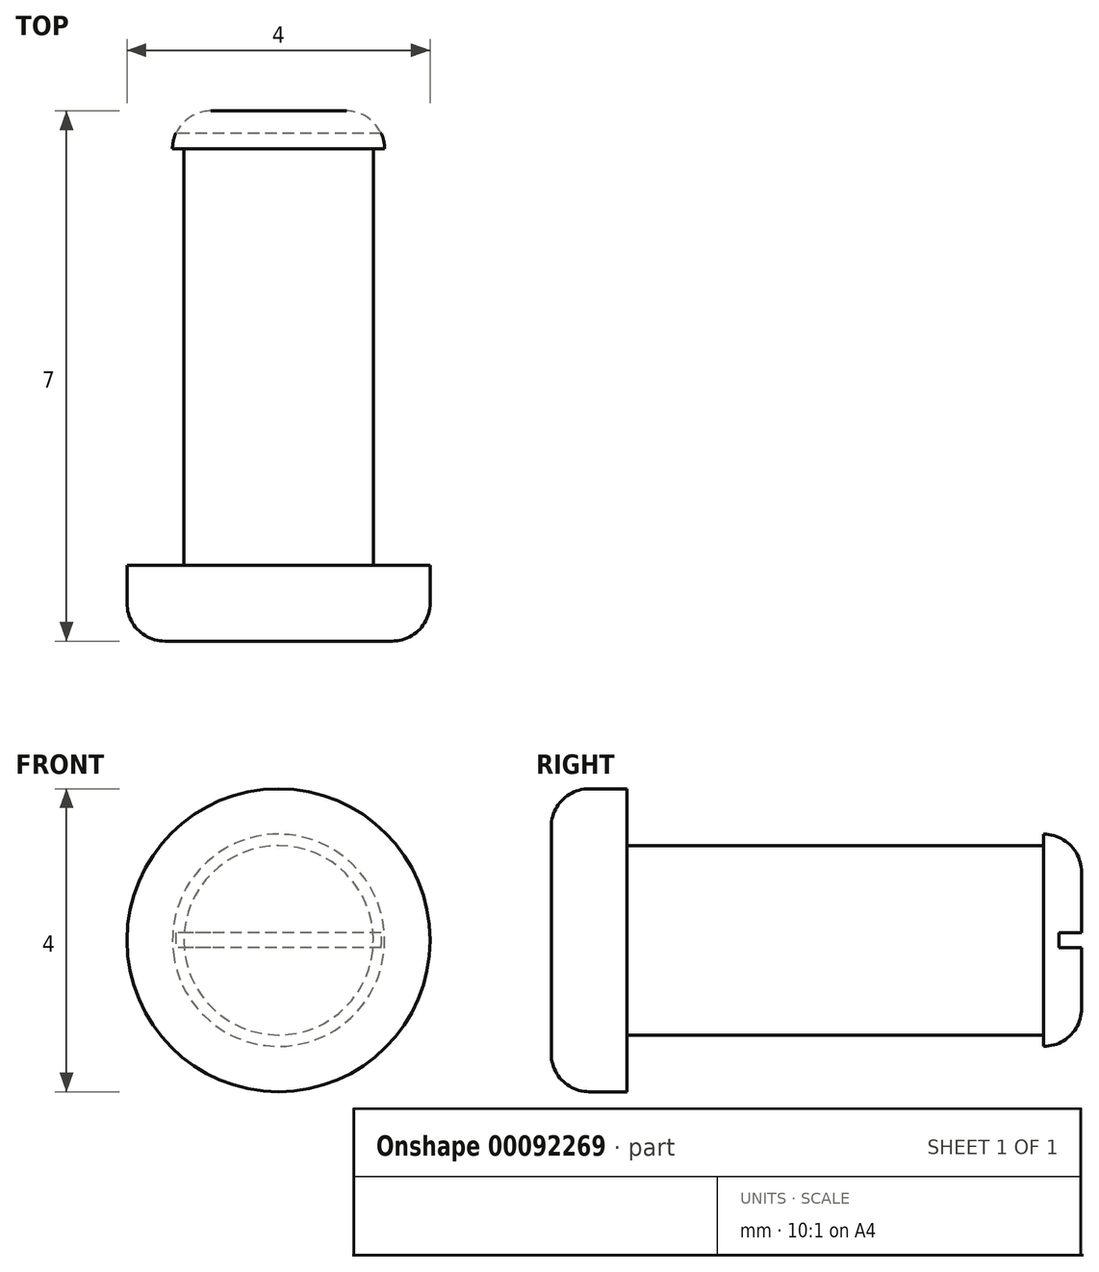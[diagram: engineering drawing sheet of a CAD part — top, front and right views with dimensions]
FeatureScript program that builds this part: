
annotation { "Feature Type Name" : "Feature", "Feature Type Description" : "" }
export const myFeature = defineFeature(function(context is Context, id is Id, definition is map)
    precondition{}
    {
        {
            var Q0;
            Q0=qCreatedBy(makeId("Right.planeOp"),FACE);
            var sketch = newSketch(context, id + "F0", { "sketchPlane" : qUnion([Q0])});
            skLineSegment(sketch, "E0", {"start": v(-2.5, 0) * mm, "end": v(3, 0) * mm});
            skLineSegment(sketch, "E1", {"start": v(3, 0) * mm, "end": v(-2.5, 0) * mm});
            skLineSegment(sketch, "E2", {"start": v(-2.5, 2) * mm, "end": v(-3.5, 2) * mm});
            skLineSegment(sketch, "E3", {"start": v(-3.5, 2) * mm, "end": v(-3.5, 0) * mm});
            skLineSegment(sketch, "E4", {"start": v(-3.5, 0) * mm, "end": v(-2.5, 0) * mm});
            skLineSegment(sketch, "E5", {"start": v(-2.5, 2) * mm, "end": v(-2.5, 1.25) * mm});
            skLineSegment(sketch, "E6", {"start": v(-2.5, 1.25) * mm, "end": v(3, 1.25) * mm});
            skLineSegment(sketch, "E7", {"start": v(3, 1.25) * mm, "end": v(3, 1.4) * mm});
            skLineSegment(sketch, "E8", {"start": v(3, 1.4) * mm, "end": v(3.5, 1.4) * mm});
            skLineSegment(sketch, "E9", {"start": v(3.5, 1.4) * mm, "end": v(3.5, 0) * mm});
            skLineSegment(sketch, "E10", {"start": v(3.5, 0) * mm, "end": v(3, 0) * mm});
            skSolve(sketch);
        }
        {
            var Q0;
            Q0 = qSketchRegion(id + "F0", true);
            var Q1;
            Q1=sQuery(id+"F0.wireOp",EDGE,"E1");
            revolve(context, id + "F1", {"entities" : qUnion([Q0]), "axis" : qUnion([Q1]), "revolveType" : RevolveType.FULL});
        }
        {
            var Q0;
            Q0=makeQuery(id+"F1.opRevolve","SWEPT_EDGE",EDGE,{"disambiguationData":[OSD([sQuery(id+"F0.wireOp",EDGE,"E2"),sQuery(id+"F0.wireOp",EDGE,"E3")])]});
            fillet(context, id + "F2", {"entities" : qUnion([Q0]), "radius" : 0.5 * mm, "tangentPropagation" : true, "allowEdgeOverflow" : false});
        }
        {
            var Q0;
            Q0=makeQuery(id+"F1.opRevolve","SWEPT_EDGE",EDGE,{"disambiguationData":[OSD([sQuery(id+"F0.wireOp",EDGE,"E8"),sQuery(id+"F0.wireOp",EDGE,"E9")])]});
            var Q1;
            Q1=makeQuery(id+"F1.opRevolve","SWEPT_FACE",FACE,{"disambiguationData":[OSD([sQuery(id+"F0.wireOp",EDGE,"E9")])]});
            fillet(context, id + "F3", {"entities" : qUnion([Q0, Q1]), "radius" : 0.5 * mm, "tangentPropagation" : true, "allowEdgeOverflow" : false});
        }
        {
            var Q0;
            Q0=makeQuery(id+"F1.opRevolve","SWEPT_FACE",FACE,{"disambiguationData":[OSD([sQuery(id+"F0.wireOp",EDGE,"E9")])]});
            var sketch = newSketch(context, id + "F4", { "sketchPlane" : qUnion([Q0])});
            skLineSegment(sketch, "E11.bottom", {"start": v(-1.5, 0) * mm, "end": v(1.5, 0) * mm});
            skLineSegment(sketch, "E11.top", {"start": v(-1.5, 0.1) * mm, "end": v(1.5, 0.1) * mm});
            skLineSegment(sketch, "E11.left", {"start": v(-1.5, 0) * mm, "end": v(-1.5, 0.1) * mm});
            skLineSegment(sketch, "E11.right", {"start": v(1.5, 0) * mm, "end": v(1.5, 0.1) * mm});
            skLineSegment(sketch, "E12.top", {"start": v(-1.5, -0.1) * mm, "end": v(1.5, -0.1) * mm});
            skLineSegment(sketch, "E12.left", {"start": v(-1.5, 0) * mm, "end": v(-1.5, -0.1) * mm});
            skLineSegment(sketch, "E12.right", {"start": v(1.5, 0) * mm, "end": v(1.5, -0.1) * mm});
            skSolve(sketch);
        }
        {
            var Q0;
            Q0 = qSketchRegion(id + "F4", true);
            extrude(context, id + "F5", {"entities" : qUnion([Q0]), "operationType" : NewBodyOperationType.REMOVE, "oppositeDirection" : true, "depth" : 0.3 * mm});
        }
    });
